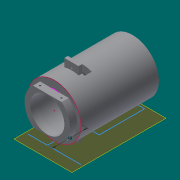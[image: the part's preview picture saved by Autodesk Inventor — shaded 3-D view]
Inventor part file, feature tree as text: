
AUTODESK INVENTOR PART (.ipt)
format: ipt  version: 2013 (Build 170138000, 138)  size: 221,184 bytes
history: native  units: mm
features: sketch x9, extrude x6, other x4, revolve x1, mirror x1
ambient origin geometry x8: Origin, YZ Plane, XZ Plane, XY Plane, X Axis, Y Axis, Z Axis, Center Point
feature tree (21):
  other  "ソリッド1"
  revolve  "回転1"
  other  "作業平面4"
  sketch  "スケッチ2"
  sketch  "スケッチ3"
  extrude  "押し出し1"  Depth=32.0mm
  extrude  "押し出し2"  Depth=30.0mm
  extrude  "押し出し3"  Depth=35.0mm
  extrude  "押し出し4"  Depth=2.0mm
  extrude  "押し出し5"  Depth=80.0mm
  mirror  "ミラー1"
  other  "作業平面5"
  extrude  "押し出し7"  TaperAngle=90.0deg  [1 undecoded]
  other  "作業平面6"
  sketch  "スケッチ9"
  sketch  "スケッチ1"
  sketch  "スケッチ4"
  sketch  "スケッチ5"
  sketch  "スケッチ6"
  sketch  "スケッチ7"
  sketch  "スケッチ8"
note: 1 required parameter value undecoded (feature->parameter linkage not recoverable at this tier; creation-order binding heuristic only, values carry confidence <= 0.55)
